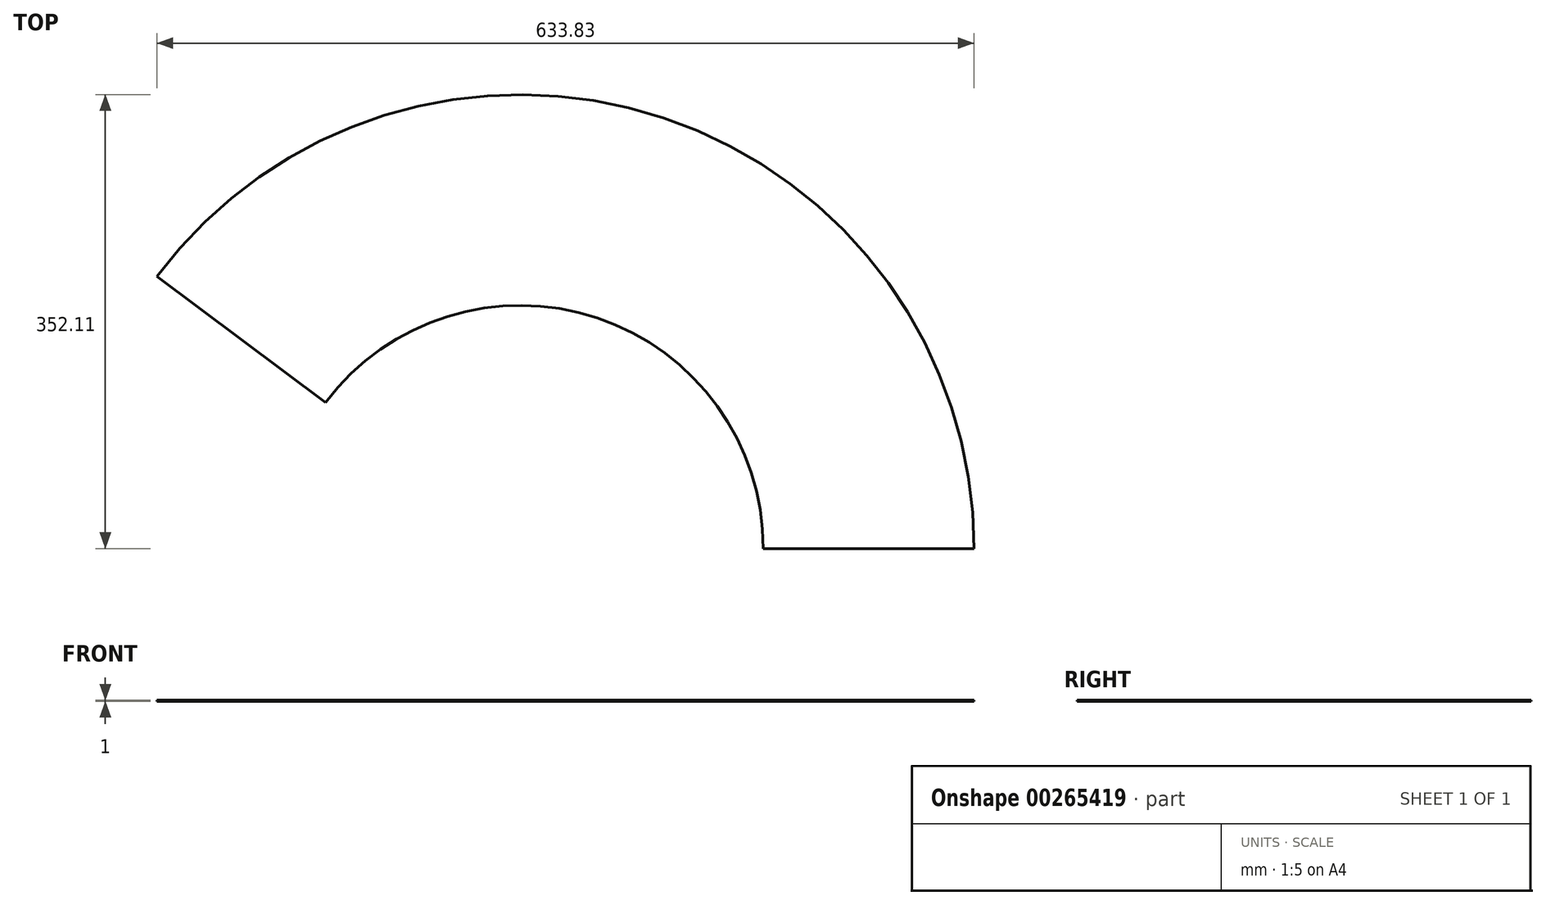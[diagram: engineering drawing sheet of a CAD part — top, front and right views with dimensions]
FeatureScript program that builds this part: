
annotation { "Feature Type Name" : "Feature", "Feature Type Description" : "" }
export const myFeature = defineFeature(function(context is Context, id is Id, definition is map)
    precondition{}
    {
        {
            var Q0;
            Q0=qCreatedBy(makeId("Top.planeOp"),FACE);
            var sketch = newSketch(context, id + "F0", { "sketchPlane" : qUnion([Q0])});
            skCircle(sketch, "E0", {"center": v(0, 0) * mm, "radius": 188.63 * mm});
            skCircle(sketch, "E1", {"center": v(0, 0) * mm, "radius": 352.1 * mm});
            skLineSegment(sketch, "E2", {"start": v(0, 0) * mm, "end": v(352.1, 0) * mm});
            skLineSegment(sketch, "E3", {"start": v(0, 0) * mm, "end": v(-281.72, 211.22) * mm});
            skSolve(sketch);
        }
        {
            var Q0;
            {var subQ0=sQuery(id+"F0.wireOp",EDGE,"E2");var subQ1=sQuery(id+"F0.wireOp",EDGE,"E0");var subQ2=makeQuery(id+"F0.imprint","INTERSECT",VERTEX,{"derivedFrom":[subQ1,subQ0]});Q0=makeQuery(id+"F0.imprint","IMPRINT",FACE,{"disambiguationData":[TD([[makeQuery(id+"F0.imprint","IMPRINT",EDGE,{"disambiguationData":[TD([[subQ2,-1.0]])],"derivedFrom":subQ1}),-1.0]])]});}
            extrude(context, id + "F1", {"entities" : qUnion([Q0]), "depth" : 1 * mm});
        }
    });
